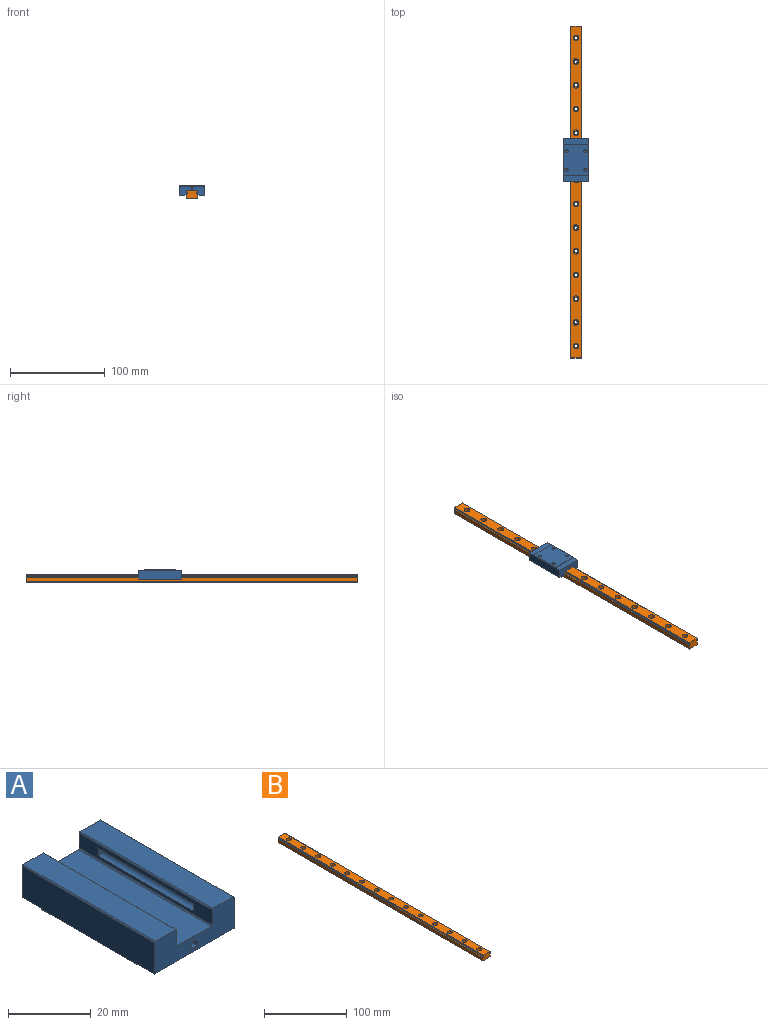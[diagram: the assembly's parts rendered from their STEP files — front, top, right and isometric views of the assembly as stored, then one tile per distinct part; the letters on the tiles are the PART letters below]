
ASSEMBLY  parts=2 mates=1
PART A: 37 faces, bbox 27x45.4x10 mm
  f0: plane 45.4x0.3mm, normal (-0.71,0,0.71), area 19.3mm2, adj f3,f6,f22,f23
  f1: plane 45.4x0.3mm, normal (0.71,0,0.71), area 19.3mm2, adj f10,f11,f22,f23
  f2: plane 45.4x0.3mm, normal (0.71,0,0.71), area 19.3mm2, adj f6,f7,f22,f23
  f3: plane 45.4x4.4mm, normal (-1,0,0), area 129.2mm2, adj f0,f5,f17,f20,f22,f23,f24
  f4: plane 45.4x11.4mm, normal (0,0,1), area 517.6mm2, adj f16,f17,f22,f23
  f5: cylinder r=1.15mm len=32.4mm, axis (0,-1,0), area 141.5mm2, adj f3,f20,f24
  f6: plane 45.4x6.9mm, normal (0,0,1), area 313.3mm2, adj f0,f2,f22,f23
  f7: plane 45.4x9.4mm, normal (1,0,0), area 424.2mm2, adj f2,f15,f18,f21,f22,f23,f25,f35
  f8: plane 32.4x26.4mm, normal (0,0,-1), area 821.1mm2, adj f14,f15,f18,f27,f29,f31,f33,f35
  f9: plane 45.4x9.4mm, normal (-1,0,0), area 424.2mm2, adj f14,f18,f21,f22,f23,f25,f34,f35
  f10: plane 45.4x6.9mm, normal (0,0,1), area 313.3mm2, adj f1,f22,f23,f34
  f11: plane 45.4x4.4mm, normal (1,0,0), area 129.2mm2, adj f1,f12,f16,f19,f22,f23,f36
  f12: cylinder r=1.15mm len=32.4mm, axis (0,-1,0), area 141.5mm2, adj f11,f19,f36
  f13: cylinder r=1mm len=45.4mm, axis (0,-1,0), area 285.3mm2, adj f22,f23
  f14: plane 32.4x0.3mm, normal (-0.71,0,-0.71), area 13.7mm2, adj f8,f9,f18,f35
  f15: plane 32.4x0.3mm, normal (0.71,0,-0.71), area 13.7mm2, adj f7,f8,f18,f35
  f16: plane 45.4x0.3mm, normal (0.71,0,0.71), area 19.3mm2, adj f4,f11,f22,f23
  f17: plane 45.4x0.3mm, normal (-0.71,0,0.71), area 19.3mm2, adj f3,f4,f22,f23
  f18: plane 27x0.5mm, normal (0,-1,0), area 13.4mm2, adj f7,f8,f9,f14,f15,f21
  f19: plane 2.3x1.52mm, normal (0,1,0), area 2.9mm2, adj f11,f12
  f20: plane 2.3x1.52mm, normal (0,1,0), area 2.9mm2, adj f3,f5
  f21: plane 27x6.5mm, normal (0,0,-1), area 175.5mm2, adj f7,f9,f18,f22
  f22: plane 27x9.5mm, normal (0,-1,0), area 193.3mm2, adj f0,f1,f2,f3,f4,f6,f7,f9
  f23: plane 27x9.5mm, normal (0,1,0), area 193.3mm2, adj f0,f1,f2,f3,f4,f6,f7,f9
  f24: plane 2.3x1.52mm, normal (0,-1,0), area 2.9mm2, adj f3,f5
  f25: plane 27x6.5mm, normal (0,0,-1), area 175.5mm2, adj f7,f9,f23,f35
  f26: cone r=857.17mm half-angle=59deg, axis (0,0,-1), area 10mm2, adj f27
  f27: cylinder r=1.65mm len=3.5mm, axis (0,0,1), area 36.3mm2, adj f8,f26
  f28: cone r=857.17mm half-angle=59deg, axis (0,0,-1), area 10mm2, adj f29
  f29: cylinder r=1.65mm len=3.5mm, axis (0,0,1), area 36.3mm2, adj f8,f28
  f30: cone r=857.17mm half-angle=59deg, axis (0,0,-1), area 10mm2, adj f31
  f31: cylinder r=1.65mm len=3.5mm, axis (0,0,1), area 36.3mm2, adj f8,f30
  f32: cone r=857.17mm half-angle=59deg, axis (0,0,-1), area 10mm2, adj f33
  f33: cylinder r=1.65mm len=3.5mm, axis (0,0,1), area 36.3mm2, adj f8,f32
  f34: plane 45.4x0.3mm, normal (-0.71,0,0.71), area 19.3mm2, adj f9,f10,f22,f23
  f35: plane 27x0.5mm, normal (0,1,0), area 13.4mm2, adj f7,f8,f9,f14,f15,f25
  f36: plane 2.3x1.52mm, normal (0,-1,0), area 2.9mm2, adj f11,f12
PART B: 64 faces, bbox 12x350x8 mm
  f0: plane 350x0.86mm, normal (1,0,0), area 301.3mm2, adj f1,f13,f62,f63
  f1: plane 350x0.35mm, normal (0.71,0,0.71), area 173.2mm2, adj f0,f2,f62,f63
  f2: plane 350x11.3mm, normal (0,0,1), area 3559.2mm2, adj f1,f3,f22,f25,f28,f31,f34,f37
  f3: plane 350x0.35mm, normal (-0.71,0,0.71), area 173.2mm2, adj f2,f4,f62,f63
  f4: plane 350x0.86mm, normal (-1,0,0), area 301.3mm2, adj f3,f14,f62,f63
  f5: plane 350x4.26mm, normal (-1,0,0), area 1491.5mm2, adj f6,f18,f62,f63
  f6: plane 350x0.35mm, normal (-0.71,0,-0.71), area 173.2mm2, adj f5,f7,f62,f63
  f7: plane 350x11.3mm, normal (0,0,-1), area 3820.3mm2, adj f6,f8,f20,f23,f26,f29,f32,f35
  f8: plane 350x0.35mm, normal (0.71,0,-0.71), area 173.2mm2, adj f7,f9,f62,f63
  f9: plane 350x4.26mm, normal (1,0,0), area 1491.5mm2, adj f8,f19,f62,f63
  f10: plane 350x0.51mm, normal (0,0,1), area 178.4mm2, adj f11,f19,f62,f63
  f11: plane 350x0.3mm, normal (1,0,0), area 105mm2, adj f10,f12,f62,f63
  f12: plane 350x0.51mm, normal (0,0,-1), area 178.4mm2, adj f11,f13,f62,f63
  f13: cylinder r=1.15mm len=350mm, axis (0,1,0), area 447.8mm2, adj f0,f12,f62,f63
  f14: cylinder r=1.15mm len=350mm, axis (0,1,0), area 447.8mm2, adj f4,f15,f62,f63
  f15: plane 350x0.51mm, normal (0,0,-1), area 178.4mm2, adj f14,f16,f62,f63
  f16: plane 350x0.3mm, normal (-1,0,0), area 105mm2, adj f15,f17,f62,f63
  f17: plane 350x0.51mm, normal (0,0,1), area 178.4mm2, adj f16,f18,f62,f63
  f18: cylinder r=1.15mm len=350mm, axis (0,1,0), area 447.8mm2, adj f5,f17,f62,f63
  f19: cylinder r=1.15mm len=350mm, axis (0,1,0), area 447.8mm2, adj f9,f10,f62,f63
  f20: cylinder r=1.75mm len=3.5mm, axis (0,0,1), area 38.5mm2, adj f7,f21
  f21: plane 6x6mm, normal (0,0,1), area 18.7mm2, adj f20,f22
  f22: cylinder r=3mm len=6mm, axis (0,0,1), area 84.8mm2, adj f2,f21
  f23: cylinder r=1.75mm len=3.5mm, axis (0,0,1), area 38.5mm2, adj f7,f24
  f24: plane 6x6mm, normal (0,0,1), area 18.7mm2, adj f23,f25
  f25: cylinder r=3mm len=6mm, axis (0,0,1), area 84.8mm2, adj f2,f24
  f26: cylinder r=1.75mm len=3.5mm, axis (0,0,1), area 38.5mm2, adj f7,f27
  f27: plane 6x6mm, normal (0,0,1), area 18.7mm2, adj f26,f28
  f28: cylinder r=3mm len=6mm, axis (0,0,1), area 84.8mm2, adj f2,f27
  f29: cylinder r=1.75mm len=3.5mm, axis (0,0,1), area 38.5mm2, adj f7,f30
  f30: plane 6x6mm, normal (0,0,1), area 18.7mm2, adj f29,f31
  f31: cylinder r=3mm len=6mm, axis (0,0,1), area 84.8mm2, adj f2,f30
  f32: cylinder r=1.75mm len=3.5mm, axis (0,0,1), area 38.5mm2, adj f7,f33
  f33: plane 6x6mm, normal (0,0,1), area 18.7mm2, adj f32,f34
  f34: cylinder r=3mm len=6mm, axis (0,0,1), area 84.8mm2, adj f2,f33
  f35: cylinder r=1.75mm len=3.5mm, axis (0,0,1), area 38.5mm2, adj f7,f36
  f36: plane 6x6mm, normal (0,0,1), area 18.7mm2, adj f35,f37
  f37: cylinder r=3mm len=6mm, axis (0,0,1), area 84.8mm2, adj f2,f36
  f38: cylinder r=1.75mm len=3.5mm, axis (0,0,1), area 38.5mm2, adj f7,f39
  f39: plane 6x6mm, normal (0,0,1), area 18.7mm2, adj f38,f40
  f40: cylinder r=3mm len=6mm, axis (0,0,1), area 84.8mm2, adj f2,f39
  f41: cylinder r=1.75mm len=3.5mm, axis (0,0,1), area 38.5mm2, adj f7,f42
  f42: plane 6x6mm, normal (0,0,1), area 18.7mm2, adj f41,f43
  f43: cylinder r=3mm len=6mm, axis (0,0,1), area 84.8mm2, adj f2,f42
  f44: cylinder r=1.75mm len=3.5mm, axis (0,0,1), area 38.5mm2, adj f7,f45
  f45: plane 6x6mm, normal (0,0,1), area 18.7mm2, adj f44,f46
  f46: cylinder r=3mm len=6mm, axis (0,0,1), area 84.8mm2, adj f2,f45
  f47: cylinder r=1.75mm len=3.5mm, axis (0,0,1), area 38.5mm2, adj f7,f48
  f48: plane 6x6mm, normal (0,0,1), area 18.7mm2, adj f47,f49
  f49: cylinder r=3mm len=6mm, axis (0,0,1), area 84.8mm2, adj f2,f48
  f50: cylinder r=1.75mm len=3.5mm, axis (0,0,1), area 38.5mm2, adj f7,f51
  f51: plane 6x6mm, normal (0,0,1), area 18.7mm2, adj f50,f52
  f52: cylinder r=3mm len=6mm, axis (0,0,1), area 84.8mm2, adj f2,f51
  f53: cylinder r=1.75mm len=3.5mm, axis (0,0,1), area 38.5mm2, adj f7,f54
  f54: plane 6x6mm, normal (0,0,1), area 18.7mm2, adj f53,f55
  f55: cylinder r=3mm len=6mm, axis (0,0,1), area 84.8mm2, adj f2,f54
  f56: cylinder r=1.75mm len=3.5mm, axis (0,0,1), area 38.5mm2, adj f7,f57
  f57: plane 6x6mm, normal (0,0,1), area 18.7mm2, adj f56,f58
  f58: cylinder r=3mm len=6mm, axis (0,0,1), area 84.8mm2, adj f2,f57
  f59: cylinder r=1.75mm len=3.5mm, axis (0,0,1), area 38.5mm2, adj f7,f60
  f60: plane 6x6mm, normal (0,0,1), area 18.7mm2, adj f59,f61
  f61: cylinder r=3mm len=6mm, axis (0,0,1), area 84.8mm2, adj f2,f60
  f62: plane 12x8mm, normal (0,1,0), area 93mm2, adj f0,f1,f2,f3,f4,f5,f6,f7
  f63: plane 12x8mm, normal (0,-1,0), area 93mm2, adj f0,f1,f2,f3,f4,f5,f6,f7
PLACE A rot(axis=(1,0,0),180deg) t=(0,17.29,0)mm
PLACE B t=(0,-175,0)mm
MATE planar A.f4 <-> B.f2  axis (0,0,-1) through (0,33.49,0)mm
